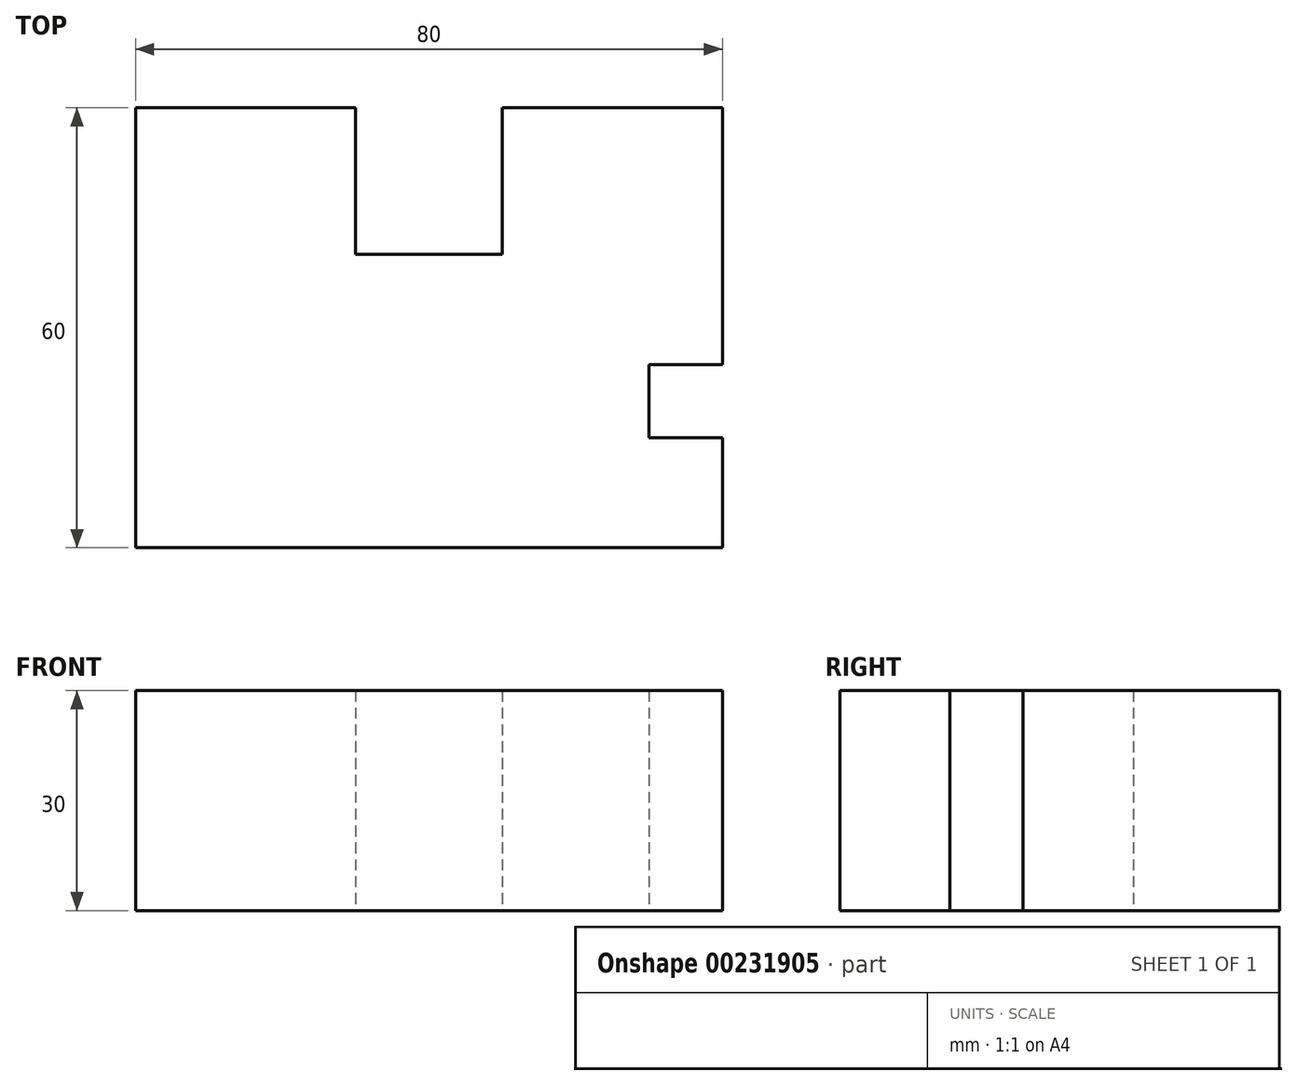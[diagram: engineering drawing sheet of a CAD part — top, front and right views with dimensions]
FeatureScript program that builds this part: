
annotation { "Feature Type Name" : "Feature", "Feature Type Description" : "" }
export const myFeature = defineFeature(function(context is Context, id is Id, definition is map)
    precondition{}
    {
        {
            var Q0;
            Q0=qCreatedBy(makeId("Top.planeOp"),FACE);
            var sketch = newSketch(context, id + "F0", { "sketchPlane" : qUnion([Q0])});
            skLineSegment(sketch, "E0", {"start": v(0, 0) * mm, "end": v(0, 60) * mm});
            skLineSegment(sketch, "E1", {"start": v(0, 60) * mm, "end": v(30, 60) * mm});
            skLineSegment(sketch, "E2", {"start": v(30, 60) * mm, "end": v(30, 40) * mm});
            skLineSegment(sketch, "E3", {"start": v(30, 40) * mm, "end": v(50, 40) * mm});
            skLineSegment(sketch, "E4", {"start": v(50, 40) * mm, "end": v(50, 60) * mm});
            skLineSegment(sketch, "E5", {"start": v(50, 60) * mm, "end": v(80, 60) * mm});
            skLineSegment(sketch, "E6", {"start": v(80, 60) * mm, "end": v(80, 25) * mm});
            skLineSegment(sketch, "E7", {"start": v(80, 25) * mm, "end": v(70, 25) * mm});
            skLineSegment(sketch, "E8", {"start": v(70, 25) * mm, "end": v(70, 15) * mm});
            skLineSegment(sketch, "E9", {"start": v(70, 15) * mm, "end": v(80, 15) * mm});
            skLineSegment(sketch, "E10", {"start": v(80, 15) * mm, "end": v(80, 0) * mm});
            skLineSegment(sketch, "E11", {"start": v(80, 0) * mm, "end": v(0, 0) * mm});
            skSolve(sketch);
        }
        {
            var Q0;
            Q0=makeQuery(id+"F0.imprint","IMPRINT",FACE,{"disambiguationData":[TD([[makeQuery(id+"F0.imprint","IMPRINT",EDGE,{"derivedFrom":sQuery(id+"F0.wireOp",EDGE,"E0")}),-1.0]])]});
            extrude(context, id + "F1", {"entities" : qUnion([Q0]), "depth" : 30 * mm});
        }
    });
